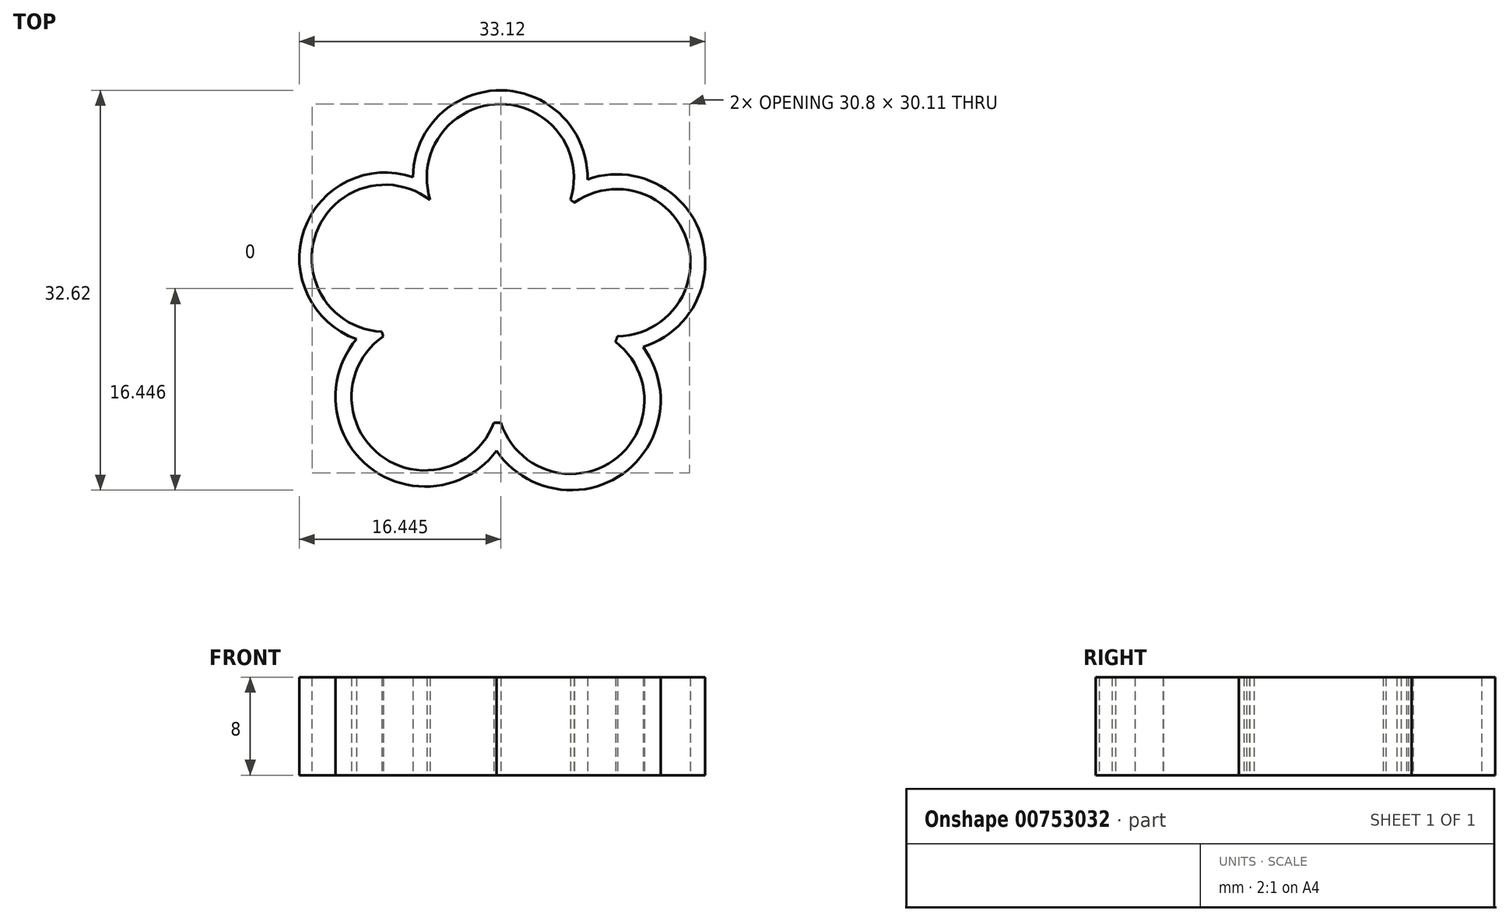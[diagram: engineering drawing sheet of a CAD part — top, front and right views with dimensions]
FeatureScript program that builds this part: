
annotation { "Feature Type Name" : "Feature", "Feature Type Description" : "" }
export const myFeature = defineFeature(function(context is Context, id is Id, definition is map)
    precondition{}
    {
        {
            var Q0;
            Q0=qCreatedBy(makeId("Top.planeOp"),FACE);
            var sketch = newSketch(context, id + "F0", { "sketchPlane" : qUnion([Q0])});
            skArc(sketch, "E0", {"start": v(-9.66, -2.57) * mm, "mid": v(-9.61, -2.76) * mm, "end": v(-9.55, -2.96) * mm});
            skArc(sketch, "E1", {"start": v(-5.7, 8.16) * mm, "mid": v(-15.03, 5.5) * mm, "end": v(-9.66, -2.57) * mm});
            skArc(sketch, "E2.trimOffspring", {"start": v(-5.72, 8.2) * mm, "mid": v(-5.73, 8.2) * mm, "end": v(-5.75, 8.18) * mm});
            skArc(sketch, "E3.trimOffspring", {"start": v(5.72, 8.2) * mm, "mid": v(-0.02, 16) * mm, "end": v(-5.7, 8.16) * mm});
            skArc(sketch, "E4.trimOffspring", {"start": v(9.56, -2.93) * mm, "mid": v(15.23, 4.9) * mm, "end": v(6.05, 7.96) * mm});
            skArc(sketch, "E5.trimOffspring", {"start": v(9.4, -3.4) * mm, "mid": v(9.48, -3.17) * mm, "end": v(9.56, -2.93) * mm});
            skArc(sketch, "E6.trimOffspring", {"start": v(6.05, 7.96) * mm, "mid": v(5.89, 8.08) * mm, "end": v(5.72, 8.2) * mm});
            skArc(sketch, "E7.trimOffspring", {"start": v(0.05, -10) * mm, "mid": v(9.22, -13.07) * mm, "end": v(9.4, -3.4) * mm});
            skArc(sketch, "E8.trimOffspring", {"start": v(-0.52, -9.99) * mm, "mid": v(-0.24, -10) * mm, "end": v(0.05, -10) * mm});
            skArc(sketch, "E9.trimOffspring", {"start": v(-9.55, -2.96) * mm, "mid": v(-9.83, -12.63) * mm, "end": v(-0.52, -9.99) * mm});
            skArc(sketch, "E10", {"start": v(-11.74, -3.18) * mm, "mid": v(-10.7, -13.61) * mm, "end": v(-0.3, -12.29) * mm});
            skArc(sketch, "E11.trimOffspring", {"start": v(-7.12, 10.04) * mm, "mid": v(-16, 5.73) * mm, "end": v(-11.74, -3.18) * mm});
            skArc(sketch, "E12.trimOffspring", {"start": v(7.12, 9.86) * mm, "mid": v(0.1, 17.12) * mm, "end": v(-7.12, 10.04) * mm});
            skArc(sketch, "E13.trimOffspring", {"start": v(11.65, -3.81) * mm, "mid": v(16.35, 5.33) * mm, "end": v(7.12, 9.86) * mm});
            skArc(sketch, "E14.trimOffspring", {"start": v(-0.3, -12.29) * mm, "mid": v(10, -14.15) * mm, "end": v(11.65, -3.81) * mm});
            skSolve(sketch);
        }
        {
            var Q0;
            {var subQ1=sQuery(id+"F0.wireOp",EDGE,"E0");Q0=makeQuery(id+"F0.imprint","IMPRINT",FACE,{"disambiguationData":[TD([[makeQuery(id+"F0.imprint","IMPRINT",EDGE,{"derivedFrom":subQ1}),-1.0]])]});}
            extrude(context, id + "F1", {"entities" : qUnion([Q0]), "depth" : 8 * mm, "offsetDistance" : 25 * mm});
        }
    });
